# Revit family: ASSA_ABLOY_MPD_RP300Wide
name_source: partatom
category: Doors
units: mm (PartAtom-declared; Revit-internal decimal feet)

## family parameters
Always vertical = Yes
Cut with Voids When Loaded = No
Host = Wall
Room Calculation Point = No
Shared = No

## types (1)
- Type 1
    AlumuniumMaterial = Aluminum
    Analytic Construction = <None>
    Area of use = Inside Or Outside
    BracketMaterial = Steel Galvanized
    ClearanceZoneHeightVD = 100 mm  [stored 0.328084 ft]
    ClearanceZoneMaterial = ASSA ABLOY Clearance Zone
    ControlBox = MCC (type 7110) or MCC, modular frequency converter control system (Vector Control)
    Description = Machine Protection Door
    Manufacturer = ASSA ABLOY
    Model = RP300Wide
    NoiseReduction = < 70 dB A
    NotChainDriveRight = Yes
    Operating speed = Opening: up to 1,7 m/s, Closing: 1,0 m/s (with safety edge)
    PVCWithVerticalStripesColor = <By Category>
    PowerSupply = 3/(N)/PE/380/400/415/440/460/480V (+/-10%), 50/60Hz
    Rolltex,NomaTexColor = <By Category>
    StainlessSteelMaterial = Steel Galvanized
    Standard = Yes
    StandardProfile = Yes
    Temperature working range = +10 °C to +45 °C
    URL = https://www.assaabloyentrance.com
    Width = 250 mm  [stored 0.82021 ft]
    Wind Resistance (EN 12424) = Class 1 (DW <= 5600 mm), Class 0 (DW > 5600 mm)

note: [stored X ft] marks values corroborated as IEEE doubles in the binary element streams (Revit-internal decimal feet)

## geometry (parser evidence)
native form markers: Sweep x24
no freeform markers — native parametric forms only
